# Revit family: PlumbingFixture_Drain_Galvin_DIR
name_source: partatom
category: Plumbing Fixtures
revit_build: Autodesk Revit MEP 2012 (Build: 20110916_2132(x64)
units: mm (PartAtom-declared; Revit-internal decimal feet)

## types (2) — shared parameters
Application = PVC/HDPE/Cu
Assembly Code = D2040200
BodyMaterial = Metal_Drains_Perforated_15400
CHWFlow_ANZRS = 2.8 L/s
Circulation_ANZRS = Yes
Description = Round Industrial  - Trap Combination
DimGrateDepth = 25 mm  [stored 0.082021 ft]
DimGrateHeight = 28 mm  [stored 0.0918635 ft]
DimOutlet = 100 mm  [stored 0.328084 ft]
DimTop = 150 mm
FilterObject_ANZRS = DIRX
GrateMaterial = Metal_Drains_Stainless-Steel_15400
Instructions = http://www.galvinengineering.com.au
Keynote = 10800
Manufacturer = Galvin Engineering
ModifiedIssue_ANZRS = 20140526 $
OutletRadius_DoNotEdit = 50 mm  [stored 0.164042 ft]
StyleOrType_ANZRS = Drain
Type Comments = Round
URL = www.galvinengineering.com.au
zero-valued in all types: Default Elevation

## per-type parameters (varying)
| type | DimGrateStrainer |
| DI4S06RX - ST/ST 316 | 92 mm  [stored 0.301837 ft] |
| DI4M06RX - ST/ST 316 | 114 mm  [stored 0.374016 ft] |

note: column(s) folded — value = type name in every type: Model

note: [stored X ft] marks values corroborated as IEEE doubles in the binary element streams (Revit-internal decimal feet)

## geometry (parser evidence)
native form markers: Blend x4, Sweep x1
no freeform markers — native parametric forms only
